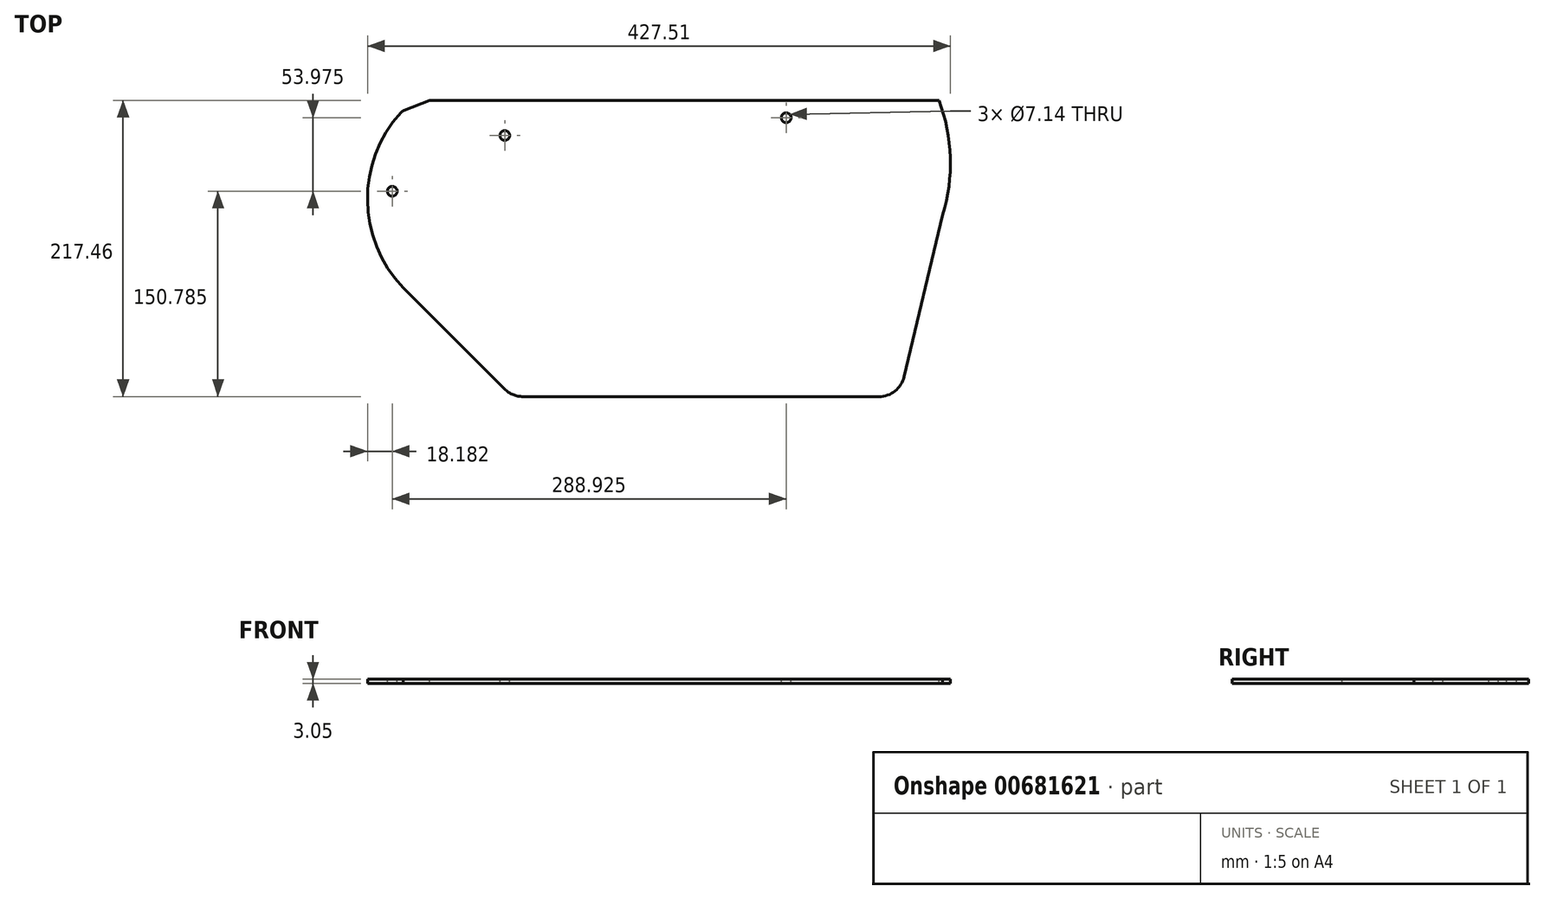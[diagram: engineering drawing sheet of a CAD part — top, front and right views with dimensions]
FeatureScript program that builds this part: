
annotation { "Feature Type Name" : "Feature", "Feature Type Description" : "" }
export const myFeature = defineFeature(function(context is Context, id is Id, definition is map)
    precondition{}
    {
        {
            var Q0;
            Q0=qCreatedBy(makeId("Top.planeOp"),FACE);
            var sketch = newSketch(context, id + "F0", { "sketchPlane" : qUnion([Q0])});
            skLineSegment(sketch, "E0", {"start": v(89.9, 293.19) * mm, "end": v(89.9, 230.84) * mm});
            skLineSegment(sketch, "E1", {"start": v(84.87, 223.45) * mm, "end": v(25.61, 200.17) * mm});
            skLineSegment(sketch, "E2", {"start": v(24.78, 70.08) * mm, "end": v(99.28, -4.42) * mm});
            skLineSegment(sketch, "E3", {"start": v(112.75, -10) * mm, "end": v(373.81, -10) * mm});
            skLineSegment(sketch, "E4", {"start": v(392.34, 4.64) * mm, "end": v(420.6, 123.35) * mm});
            skLineSegment(sketch, "E5", {"start": v(89.9, 293.19) * mm, "end": v(356.6, 293.19) * mm});
            skLineSegment(sketch, "E6", {"start": v(356.6, 293.19) * mm, "end": v(356.6, 277.31) * mm});
            skPoint(sketch, "E7.visualSharp", {"position": v(89.9, 225.43) * mm});
            skArc(sketch, "E7.filletArc", {"start": v(84.87, 223.45) * mm, "mid": v(88.53, 226.37) * mm, "end": v(89.9, 230.84) * mm});
            skPoint(sketch, "E8.startSnap0", {"position": v(0, 142.48) * mm});
            skArc(sketch, "E9.0", {"start": v(23.24, 198.54) * mm, "mid": v(-1.3, 134) * mm, "end": v(24.78, 70.08) * mm});
            skPoint(sketch, "E10.visualSharp", {"position": v(104.85, -10) * mm});
            skArc(sketch, "E10.filletArc", {"start": v(99.28, -4.42) * mm, "mid": v(105.46, -8.55) * mm, "end": v(112.75, -10) * mm});
            skPoint(sketch, "E11.visualSharp", {"position": v(388.86, -10) * mm});
            skArc(sketch, "E11.filletArc", {"start": v(373.81, -10) * mm, "mid": v(385.62, -5.9) * mm, "end": v(392.34, 4.64) * mm});
            skArc(sketch, "E12", {"start": v(420.6, 123.35) * mm, "mid": v(416.15, 211.78) * mm, "end": v(356.6, 277.31) * mm});
            skPoint(sketch, "E13.visualSharp", {"position": v(24.26, 199.64) * mm});
            skArc(sketch, "E13.filletArc", {"start": v(25.61, 200.17) * mm, "mid": v(24.33, 199.49) * mm, "end": v(23.24, 198.54) * mm});
            skSolve(sketch);
        }
        {
            var Q0;
            Q0=makeQuery(id+"F0.imprint","IMPRINT",FACE,{"disambiguationData":[TD([[makeQuery(id+"F0.imprint","IMPRINT",EDGE,{"derivedFrom":sQuery(id+"F0.wireOp",EDGE,"E0")}),1.0]])]});
            extrude(context, id + "F1", {"entities" : qUnion([Q0]), "depth" : 3.05 * mm, "offsetDistance" : 25.4 * mm});
        }
        {
            var Q0;
            Q0=makeQuery(id+"F1.opExtrude","CAP_FACE",FACE,{"disambiguationData":[OSD([sQuery(id+"F0.wireOp",EDGE,"E0"),sQuery(id+"F0.wireOp",EDGE,"E1"),sQuery(id+"F0.wireOp",EDGE,"E2"),sQuery(id+"F0.wireOp",EDGE,"E3"),sQuery(id+"F0.wireOp",EDGE,"E4"),sQuery(id+"F0.wireOp",EDGE,"E5"),sQuery(id+"F0.wireOp",EDGE,"E6"),sQuery(id+"F0.wireOp",EDGE,"E7.filletArc"),sQuery(id+"F0.wireOp",EDGE,"E9.0"),sQuery(id+"F0.wireOp",EDGE,"E10.filletArc"),sQuery(id+"F0.wireOp",EDGE,"E11.filletArc"),sQuery(id+"F0.wireOp",EDGE,"E12")])],"isStart":false});
            var sketch = newSketch(context, id + "F2", { "sketchPlane" : qUnion([Q0])});
            skCircle(sketch, "E14", {"center": v(261.36, 283.66) * mm, "radius": 2.38 * mm});
            skCircle(sketch, "E15", {"center": v(197.86, 283.66) * mm, "radius": 2.38 * mm});
            skCircle(sketch, "E16", {"center": v(134.36, 283.66) * mm, "radius": 2.38 * mm});
            skSolve(sketch);
        }
        {
            var Q0;
            Q0=qSketchRegion(id+"F2",true);
            extrude(context, id + "F3", {"entities" : qUnion([Q0]), "operationType" : NewBodyOperationType.REMOVE, "endBound" : BoundingType.UP_TO_NEXT, "oppositeDirection" : true, "depth" : 25.4 * mm});
        }
        {
            var Q0;
            Q0=makeQuery(id+"F1.opExtrude","CAP_FACE",FACE,{"disambiguationData":[OSD([sQuery(id+"F0.wireOp",EDGE,"E0"),sQuery(id+"F0.wireOp",EDGE,"E1"),sQuery(id+"F0.wireOp",EDGE,"E2"),sQuery(id+"F0.wireOp",EDGE,"E3"),sQuery(id+"F0.wireOp",EDGE,"E4"),sQuery(id+"F0.wireOp",EDGE,"E5"),sQuery(id+"F0.wireOp",EDGE,"E6"),sQuery(id+"F0.wireOp",EDGE,"E7.filletArc"),sQuery(id+"F0.wireOp",EDGE,"E9.0"),sQuery(id+"F0.wireOp",EDGE,"E10.filletArc"),sQuery(id+"F0.wireOp",EDGE,"E11.filletArc"),sQuery(id+"F0.wireOp",EDGE,"E12"),sQuery(id+"F0.wireOp",EDGE,"E13.filletArc")])],"isStart":false});
            var sketch = newSketch(context, id + "F4", { "sketchPlane" : qUnion([Q0])});
            skCircle(sketch, "E17", {"center": v(99.43, 181.66) * mm, "radius": 3.57 * mm});
            skCircle(sketch, "E18", {"center": v(16.88, 140.79) * mm, "radius": 3.57 * mm});
            skCircle(sketch, "E19", {"center": v(305.8, 194.76) * mm, "radius": 3.57 * mm});
            skSolve(sketch);
        }
        {
            var Q0;
            Q0=qSketchRegion(id+"F4",true);
            extrude(context, id + "F5", {"entities" : qUnion([Q0]), "operationType" : NewBodyOperationType.REMOVE, "oppositeDirection" : true, "depth" : 9.52 * mm, "offsetDistance" : 25.4 * mm});
        }
        {
            var Q0;
            Q0=makeQuery(id+"F1.opExtrude","CAP_FACE",FACE,{"disambiguationData":[OSD([sQuery(id+"F0.wireOp",EDGE,"E0"),sQuery(id+"F0.wireOp",EDGE,"E1"),sQuery(id+"F0.wireOp",EDGE,"E2"),sQuery(id+"F0.wireOp",EDGE,"E3"),sQuery(id+"F0.wireOp",EDGE,"E4"),sQuery(id+"F0.wireOp",EDGE,"E5"),sQuery(id+"F0.wireOp",EDGE,"E6"),sQuery(id+"F0.wireOp",EDGE,"E7.filletArc"),sQuery(id+"F0.wireOp",EDGE,"E9.0"),sQuery(id+"F0.wireOp",EDGE,"E10.filletArc"),sQuery(id+"F0.wireOp",EDGE,"E11.filletArc"),sQuery(id+"F0.wireOp",EDGE,"E12"),sQuery(id+"F0.wireOp",EDGE,"E13.filletArc")])],"isStart":false});
            var sketch = newSketch(context, id + "F6", { "sketchPlane" : qUnion([Q0])});
            skLineSegment(sketch, "E20", {"start": v(417.85, 207.46) * mm, "end": v(44.17, 207.46) * mm});
            skSolve(sketch);
        }
        {
            var Q0;
            Q0=makeQuery(id+"F6.imprint","IMPRINT",FACE,{"disambiguationData":[TD([[makeQuery(id+"F6.imprint","IMPRINT",EDGE,{"derivedFrom":makeQuery(id+"F1.opExtrude","CAP_EDGE",EDGE,{"disambiguationData":[OSD([sQuery(id+"F0.wireOp",EDGE,"E0")])],"isStart":false})}),1.0]])]});
            extrude(context, id + "F7", {"entities" : qUnion([Q0]), "operationType" : NewBodyOperationType.REMOVE, "oppositeDirection" : true, "depth" : 6.35 * mm, "offsetDistance" : 25.4 * mm});
        }
    });
